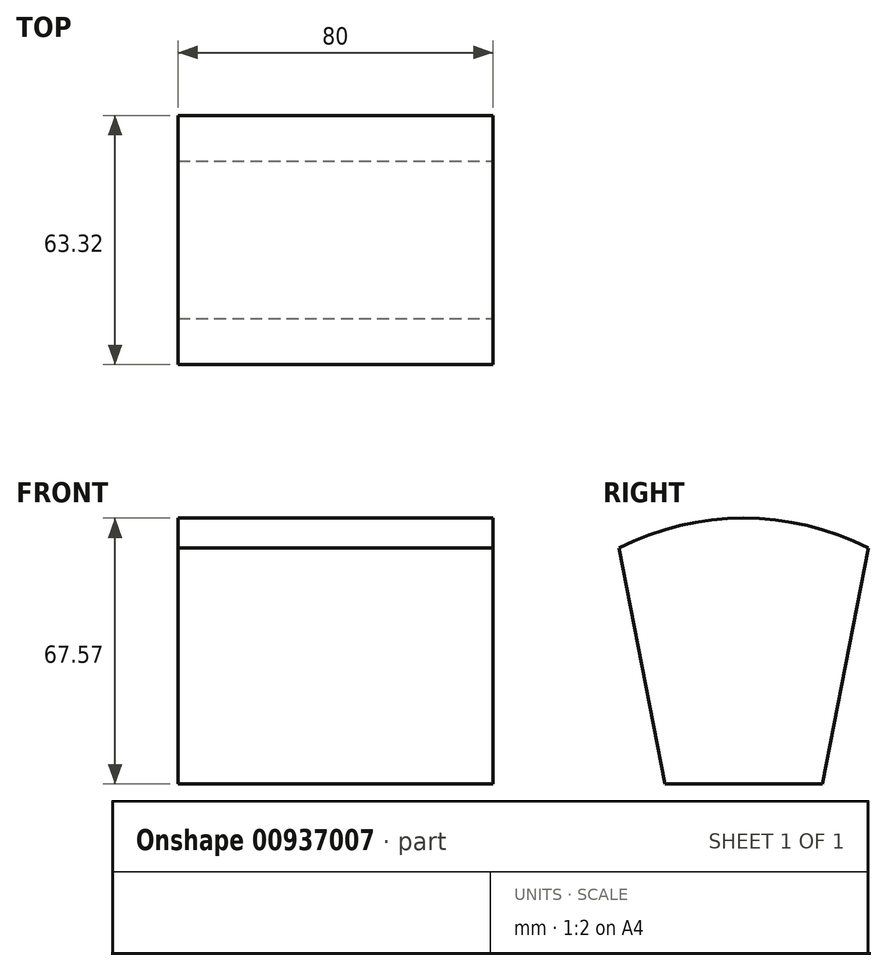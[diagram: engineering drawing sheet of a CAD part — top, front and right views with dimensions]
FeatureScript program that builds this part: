
annotation { "Feature Type Name" : "Feature", "Feature Type Description" : "" }
export const myFeature = defineFeature(function(context is Context, id is Id, definition is map)
    precondition{}
    {
        {
            var Q0;
            Q0=qCreatedBy(makeId("Right.planeOp"),FACE);
            var sketch = newSketch(context, id + "F0", { "sketchPlane" : qUnion([Q0])});
            skLineSegment(sketch, "E0", {"start": v(0, 0) * mm, "end": v(0, 59.62) * mm, "construction": true});
            skLineSegment(sketch, "E1", {"start": v(0, 0) * mm, "end": v(70.09, 0) * mm, "construction": true});
            skArc(sketch, "E2", {"start": v(31.66, 60) * mm, "mid": v(0, 67.57) * mm, "end": v(-31.66, 60) * mm});
            skLineSegment(sketch, "E3", {"start": v(31.66, 60) * mm, "end": v(20, 0) * mm});
            skLineSegment(sketch, "E4", {"start": v(20, 0) * mm, "end": v(-20, 0) * mm});
            skLineSegment(sketch, "E5", {"start": v(-20, 0) * mm, "end": v(-31.66, 60) * mm});
            skSolve(sketch);
        }
        {
            var Q0;
            Q0=makeQuery(id+"F0.imprint","IMPRINT",FACE,{"disambiguationData":[TD([[makeQuery(id+"F0.imprint","IMPRINT",EDGE,{"derivedFrom":sQuery(id+"F0.wireOp",EDGE,"E2")}),1.0]])]});
            extrude(context, id + "F1", {"entities" : qUnion([Q0]), "oppositeDirection" : true, "depth" : 80 * mm, "offsetDistance" : 25 * mm});
        }
    });
